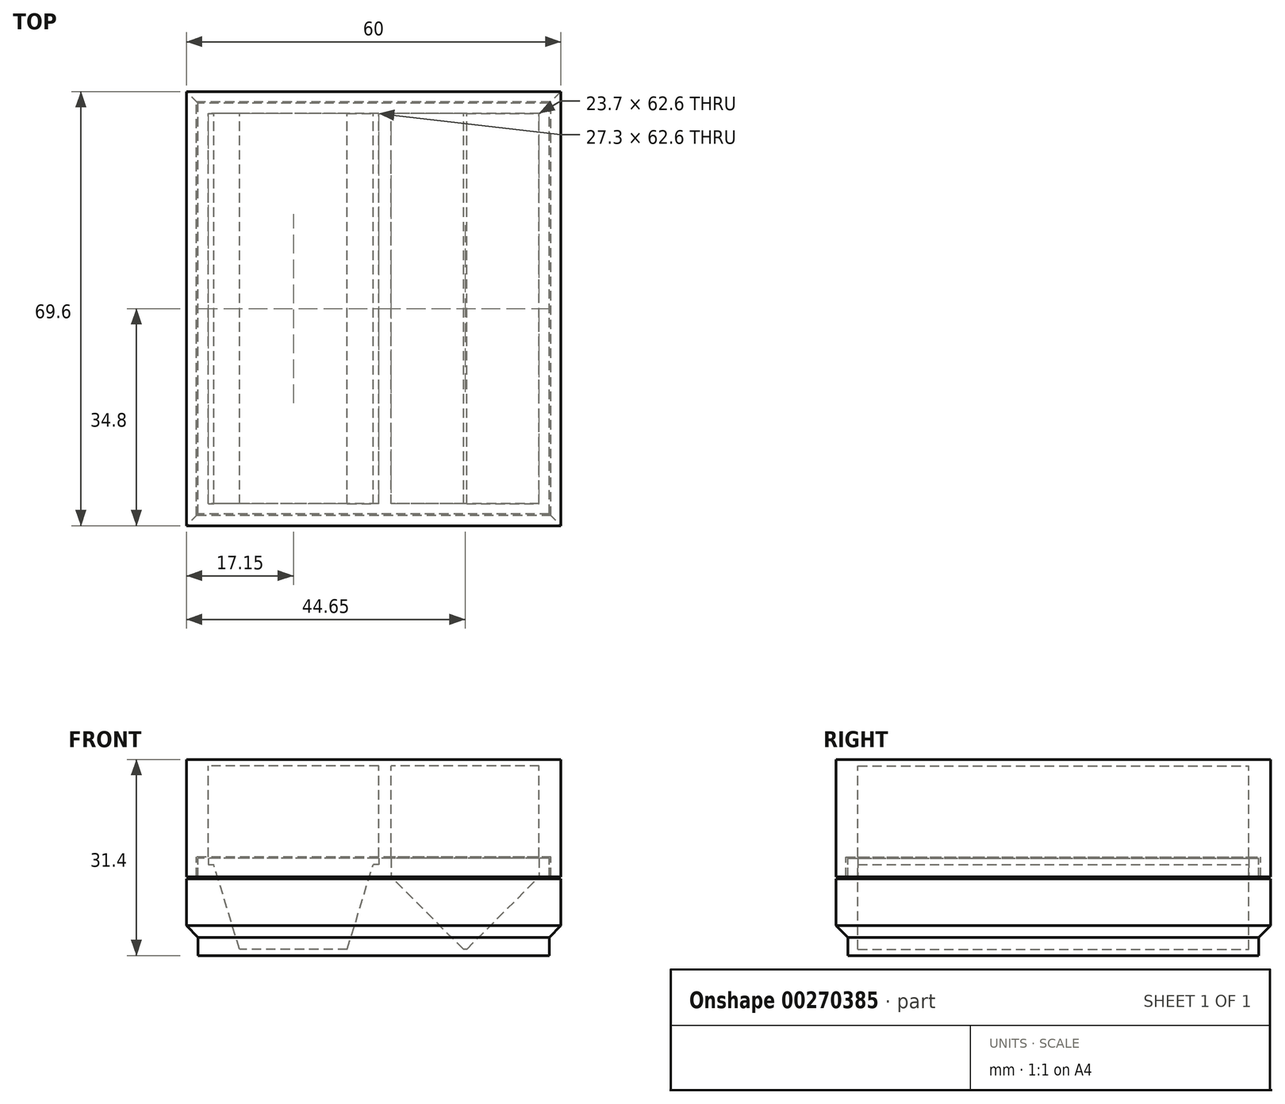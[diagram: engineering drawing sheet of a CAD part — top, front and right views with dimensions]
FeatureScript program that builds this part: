
annotation { "Feature Type Name" : "Feature", "Feature Type Description" : "" }
export const myFeature = defineFeature(function(context is Context, id is Id, definition is map)
    precondition{}
    {
        {
            assignVariable(context, id + "F0", {"name" : "chaff", "anyValue" : .3});
        }
        {
            assignVariable(context, id + "F1", {"name" : "basethick", "anyValue" : 1});
        }
        {
            assignVariable(context, id + "F2", {"name" : "wallthick", "anyValue" : 3.5});
        }
        {
            assignVariable(context, id + "F3", {"name" : "fiveTokenHeight", "anyValue" : 28});
        }
        {
            assignVariable(context, id + "F4", {"name" : "lidrimthick", "anyValue" : getVariable(context, 'wallthick') / 2 + (getVariable(context, 'chaff') / 2)});
        }
        {
            assignVariable(context, id + "F5", {"name" : "lidrimdepth", "anyValue" : 3});
        }
        {
            var Q0;
            Q0=qCreatedBy(makeId("Top.planeOp"),FACE);
            var sketch = newSketch(context, id + "F6", { "sketchPlane" : qUnion([Q0])});
            skLineSegment(sketch, "E0.bottom", {"start": v(30, -34.8) * mm, "end": v(-30, -34.8) * mm});
            skLineSegment(sketch, "E0.top", {"start": v(30, 34.8) * mm, "end": v(-30, 34.8) * mm});
            skLineSegment(sketch, "E0.left", {"start": v(30, -34.8) * mm, "end": v(30, 34.8) * mm});
            skLineSegment(sketch, "E0.right", {"start": v(-30, -34.8) * mm, "end": v(-30, 34.8) * mm});
            skPoint(sketch, "E0.middle", {"position": v(0, 0) * mm});
            skSolve(sketch);
        }
        {
            var Q0;
            Q0=qSketchRegion(id+"F6",true);
            extrude(context, id + "F7", {"entities" : qUnion([Q0]), "depth" : (getVariable(context, 'basethick')) * mm});
        }
        {
            var Q0;
            Q0=makeQuery(id+"F7.opExtrude","CAP_FACE",FACE,{"disambiguationData":[OSD([sQuery(id+"F6.wireOp",EDGE,"E0.bottom"),sQuery(id+"F6.wireOp",EDGE,"E0.top"),sQuery(id+"F6.wireOp",EDGE,"E0.left"),sQuery(id+"F6.wireOp",EDGE,"E0.right")])],"isStart":false});
            var sketch = newSketch(context, id + "F8", { "sketchPlane" : qUnion([Q0])});
            skLineSegment(sketch, "E1.bottom", {"start": v(26.5, -31.3) * mm, "end": v(-26.5, -31.3) * mm});
            skLineSegment(sketch, "E1.top", {"start": v(26.5, 31.3) * mm, "end": v(-26.5, 31.3) * mm});
            skLineSegment(sketch, "E1.left", {"start": v(26.5, -31.3) * mm, "end": v(26.5, 31.3) * mm});
            skLineSegment(sketch, "E1.right", {"start": v(-26.5, -31.3) * mm, "end": v(-26.5, 31.3) * mm});
            skPoint(sketch, "E1.middle", {"position": v(0, 0) * mm});
            skLineSegment(sketch, "E2", {"start": v(0, 31.3) * mm, "end": v(0, 34.8) * mm, "construction": true});
            skLineSegment(sketch, "E3.0", {"start": v(-30, -34.8) * mm, "end": v(-30, 34.8) * mm});
            skLineSegment(sketch, "E4.0", {"start": v(30, -34.8) * mm, "end": v(-30, -34.8) * mm});
            skLineSegment(sketch, "E5.0", {"start": v(30, -34.8) * mm, "end": v(30, 34.8) * mm});
            skLineSegment(sketch, "E6.0", {"start": v(30, 34.8) * mm, "end": v(-30, 34.8) * mm});
            skLineSegment(sketch, "E7", {"start": v(-30, 0) * mm, "end": v(-26.5, 0) * mm, "construction": true});
            skSolve(sketch);
        }
        {
            var Q0;
            Q0=qSketchRegion(id+"F8",true);
            extrude(context, id + "F9", {"entities" : qUnion([Q0]), "operationType" : NewBodyOperationType.ADD, "depth" : (getVariable(context, 'fiveTokenHeight') / 2 + getVariable(context, 'chaff') * 2) * mm});
        }
        {
            var Q0;
            Q0=makeQuery(id+"F9.opExtrude","SWEPT_FACE",FACE,{"disambiguationData":[OSD([sQuery(id+"F8.wireOp",EDGE,"E1.top")])]});
            var sketch = newSketch(context, id + "F10", { "sketchPlane" : qUnion([Q0])});
            skLineSegment(sketch, "E8", {"start": v(-26.5, 15.6) * mm, "end": v(0.8, 15.6) * mm, "construction": true});
            skLineSegment(sketch, "E9.bottom", {"start": v(0.8, 15.6) * mm, "end": v(2.8, 15.6) * mm});
            skLineSegment(sketch, "E9.top", {"start": v(0.8, 1) * mm, "end": v(2.8, 1) * mm});
            skLineSegment(sketch, "E9.left", {"start": v(0.8, 15.6) * mm, "end": v(0.8, 1) * mm});
            skLineSegment(sketch, "E9.right", {"start": v(2.8, 15.6) * mm, "end": v(2.8, 1) * mm});
            skLineSegment(sketch, "E10", {"start": v(2.8, 15.6) * mm, "end": v(26.5, 15.6) * mm, "construction": true});
            skLineSegment(sketch, "E11", {"start": v(-21.47, 1) * mm, "end": v(-4.22, 1) * mm});
            skPoint(sketch, "E12", {"position": v(-12.85, 1) * mm});
            skLineSegment(sketch, "E13", {"start": v(-12.85, 15.6) * mm, "end": v(-12.85, 1) * mm, "construction": true});
            skLineSegment(sketch, "E14", {"start": v(-21.47, 1) * mm, "end": v(-26.5, 1) * mm});
            skLineSegment(sketch, "E15", {"start": v(-26.5, 1) * mm, "end": v(-26.5, 15.6) * mm});
            skLineSegment(sketch, "E16", {"start": v(0.8, 1) * mm, "end": v(-4.22, 1) * mm});
            skLineSegment(sketch, "E17", {"start": v(14.65, 15.6) * mm, "end": v(14.65, 1) * mm, "construction": true});
            skLineSegment(sketch, "E18", {"start": v(14.4, 1) * mm, "end": v(14.9, 1) * mm});
            skLineSegment(sketch, "E19", {"start": v(14.4, 1) * mm, "end": v(2.8, 12.6) * mm});
            skLineSegment(sketch, "E20", {"start": v(14.9, 1) * mm, "end": v(26.5, 12.6) * mm});
            skLineSegment(sketch, "E21", {"start": v(2.8, 1) * mm, "end": v(14.4, 1) * mm});
            skLineSegment(sketch, "E22", {"start": v(14.9, 1) * mm, "end": v(26.5, 1) * mm});
            skLineSegment(sketch, "E23", {"start": v(26.5, 1) * mm, "end": v(26.5, 12.6) * mm});
            skLineSegment(sketch, "E24", {"start": v(-21.47, 1) * mm, "end": v(-26.5, 17.5) * mm});
            skLineSegment(sketch, "E25", {"start": v(-4.22, 1) * mm, "end": v(0.8, 17.5) * mm});
            skLineSegment(sketch, "E26", {"start": v(-26.5, 14.6) * mm, "end": v(-25.62, 14.6) * mm});
            skLineSegment(sketch, "E27", {"start": v(-26.5, 15.6) * mm, "end": v(-26.5, 14.6) * mm, "construction": true});
            skLineSegment(sketch, "E28.MirrorCS", {"start": v(0.8, 14.6) * mm, "end": v(-0.08, 14.6) * mm});
            skSolve(sketch);
        }
        {
            var Q0;
            {var subQ4=sQuery(id+"F10.wireOp",EDGE,"E9.bottom");Q0=makeQuery(id+"F10.imprint","IMPRINT",FACE,{"disambiguationData":[TD([[makeQuery(id+"F10.imprint","IMPRINT",EDGE,{"derivedFrom":subQ4}),1.0]])]});}
            var Q1;
            Q1=makeQuery(id+"F9.opExtrude","SWEPT_FACE",FACE,{"disambiguationData":[OSD([sQuery(id+"F8.wireOp",EDGE,"E1.bottom")])]});
            extrude(context, id + "F11", {"entities" : qUnion([Q0]), "operationType" : NewBodyOperationType.ADD, "endBound" : BoundingType.UP_TO_SURFACE, "endBoundEntityFace" : qUnion([Q1]), "depth" : 25 * mm});
        }
        {
            var Q0;
            {var subQ0=sQuery(id+"F10.wireOp",EDGE,"b7063ba6-163c-4e90-9692-3a0a1676d49b.0");var subQ1=sQuery(id+"F10.wireOp",EDGE,"5b0bd29a-2a72-4641-92b4-ce3cebaaf724.1.0.1");var subQ2=sQuery(id+"F10.wireOp",EDGE,"5b0bd29a-2a72-4641-92b4-ce3cebaaf724.2.0.1");Q0=makeQuery(id+"F11.boolean.opBoolean","MERGE",FACE,{"derivedFrom":[makeQuery(id+"F9.opExtrude","CAP_FACE",FACE,{"disambiguationData":[OSD([sQuery(id+"F8.wireOp",EDGE,"E1.bottom"),sQuery(id+"F8.wireOp",EDGE,"E1.top"),sQuery(id+"F8.wireOp",EDGE,"E1.left"),sQuery(id+"F8.wireOp",EDGE,"E1.right"),sQuery(id+"F8.wireOp",EDGE,"E3.0"),sQuery(id+"F8.wireOp",EDGE,"E4.0"),sQuery(id+"F8.wireOp",EDGE,"E5.0"),sQuery(id+"F8.wireOp",EDGE,"E6.0")])],"isStart":false}),makeQuery(id+"F11.opExtrude","SWEPT_FACE",FACE,{"disambiguationData":[OSD([subQ0]),TDD([makeQuery(id+"F10.imprint","IMPRINT",EDGE,{"disambiguationData":[TD([[makeQuery(id+"F10.imprint","INTERSECT",VERTEX,{"derivedFrom":[sQuery(id+"F10.wireOp",EDGE,"ed8556cc-012e-414f-a647-4d99696943b9.0"),subQ0]}),-1.0]])],"derivedFrom":subQ0})])]}),makeQuery(id+"F11.opExtrude","SWEPT_FACE",FACE,{"disambiguationData":[OSD([subQ0]),TDD([makeQuery(id+"F10.imprint","IMPRINT",EDGE,{"disambiguationData":[TD([[makeQuery(id+"F10.imprint","INTERSECT",VERTEX,{"disambiguationData":[OD(1.0)],"derivedFrom":[subQ2,subQ0]}),1.0]])],"derivedFrom":subQ0})])]}),makeQuery(id+"F11.opExtrude","SWEPT_FACE",FACE,{"disambiguationData":[OSD([subQ0]),TDD([makeQuery(id+"F10.imprint","IMPRINT",EDGE,{"disambiguationData":[TD([[makeQuery(id+"F10.imprint","INTERSECT",VERTEX,{"disambiguationData":[OD(1.0)],"derivedFrom":[subQ1,subQ0]}),1.0]])],"derivedFrom":subQ0})])]}),makeQuery(id+"F11.opExtrude","SWEPT_FACE",FACE,{"disambiguationData":[OSD([subQ0]),TDD([makeQuery(id+"F10.imprint","IMPRINT",EDGE,{"disambiguationData":[TD([[makeQuery(id+"F10.imprint","INTERSECT",VERTEX,{"derivedFrom":[sQuery(id+"F10.wireOp",EDGE,"CCxmkI6E-hdHg-CZTa-q9Gf-agiM700yoBqG"),subQ0]}),1.0]])],"derivedFrom":subQ0})])]})]});}
            cPlane(context, id + "F12", {"entities" : qUnion([Q0]), "cplaneType" : CPlaneType.OFFSET, "offset" : .1 * mm, "width" : 150 * mm, "height" : 150 * mm});
        }
        {
            var Q0;
            Q0=makeQuery(id+"F7.opExtrude","SWEPT_BODY",BODY,{"disambiguationData":[OSD([sQuery(id+"F6.wireOp",EDGE,"E0.bottom"),sQuery(id+"F6.wireOp",EDGE,"E0.top"),sQuery(id+"F6.wireOp",EDGE,"E0.left"),sQuery(id+"F6.wireOp",EDGE,"E0.right")])]});
            var Q1;
            Q1=qCreatedBy(id+"F12.planeOp",FACE);
            mirror(context, id + "F13", {"entities" : qUnion([Q0]), "mirrorPlane" : qUnion([Q1])});
        }
        {
            var Q0;
            {var subQ0=sQuery(id+"F10.wireOp",EDGE,"b7063ba6-163c-4e90-9692-3a0a1676d49b.0");var subQ1=sQuery(id+"F10.wireOp",EDGE,"5b0bd29a-2a72-4641-92b4-ce3cebaaf724.1.0.1");var subQ2=sQuery(id+"F10.wireOp",EDGE,"5b0bd29a-2a72-4641-92b4-ce3cebaaf724.2.0.1");Q0=makeQuery(id+"F11.boolean.opBoolean","MERGE",FACE,{"derivedFrom":[makeQuery(id+"F9.opExtrude","CAP_FACE",FACE,{"disambiguationData":[OSD([sQuery(id+"F8.wireOp",EDGE,"E1.bottom"),sQuery(id+"F8.wireOp",EDGE,"E1.top"),sQuery(id+"F8.wireOp",EDGE,"E1.left"),sQuery(id+"F8.wireOp",EDGE,"E1.right"),sQuery(id+"F8.wireOp",EDGE,"E3.0"),sQuery(id+"F8.wireOp",EDGE,"E4.0"),sQuery(id+"F8.wireOp",EDGE,"E5.0"),sQuery(id+"F8.wireOp",EDGE,"E6.0")])],"isStart":false}),makeQuery(id+"F11.opExtrude","SWEPT_FACE",FACE,{"disambiguationData":[OSD([subQ0]),TDD([makeQuery(id+"F10.imprint","IMPRINT",EDGE,{"disambiguationData":[TD([[makeQuery(id+"F10.imprint","INTERSECT",VERTEX,{"derivedFrom":[sQuery(id+"F10.wireOp",EDGE,"ed8556cc-012e-414f-a647-4d99696943b9.0"),subQ0]}),-1.0]])],"derivedFrom":subQ0})])]}),makeQuery(id+"F11.opExtrude","SWEPT_FACE",FACE,{"disambiguationData":[OSD([subQ0]),TDD([makeQuery(id+"F10.imprint","IMPRINT",EDGE,{"disambiguationData":[TD([[makeQuery(id+"F10.imprint","INTERSECT",VERTEX,{"disambiguationData":[OD(1.0)],"derivedFrom":[subQ2,subQ0]}),1.0]])],"derivedFrom":subQ0})])]}),makeQuery(id+"F11.opExtrude","SWEPT_FACE",FACE,{"disambiguationData":[OSD([subQ0]),TDD([makeQuery(id+"F10.imprint","IMPRINT",EDGE,{"disambiguationData":[TD([[makeQuery(id+"F10.imprint","INTERSECT",VERTEX,{"disambiguationData":[OD(1.0)],"derivedFrom":[subQ1,subQ0]}),1.0]])],"derivedFrom":subQ0})])]}),makeQuery(id+"F11.opExtrude","SWEPT_FACE",FACE,{"disambiguationData":[OSD([subQ0]),TDD([makeQuery(id+"F10.imprint","IMPRINT",EDGE,{"disambiguationData":[TD([[makeQuery(id+"F10.imprint","INTERSECT",VERTEX,{"derivedFrom":[sQuery(id+"F10.wireOp",EDGE,"CCxmkI6E-hdHg-CZTa-q9Gf-agiM700yoBqG"),subQ0]}),1.0]])],"derivedFrom":subQ0})])]})]});}
            var sketch = newSketch(context, id + "F14", { "sketchPlane" : qUnion([Q0])});
            skLineSegment(sketch, "E29.0", {"start": v(30, 34.8) * mm, "end": v(-30, 34.8) * mm});
            skLineSegment(sketch, "E30.0", {"start": v(-30, -34.8) * mm, "end": v(-30, 34.8) * mm});
            skLineSegment(sketch, "E31.0", {"start": v(30, -34.8) * mm, "end": v(-30, -34.8) * mm});
            skLineSegment(sketch, "E32.0", {"start": v(30, -34.8) * mm, "end": v(30, 34.8) * mm});
            skLineSegment(sketch, "E33.0", {"start": v(28.1, 32.9) * mm, "end": v(-28.1, 32.9) * mm});
            skLineSegment(sketch, "E33.1", {"start": v(28.1, -32.9) * mm, "end": v(28.1, 32.9) * mm});
            skLineSegment(sketch, "E33.2", {"start": v(28.1, -32.9) * mm, "end": v(-28.1, -32.9) * mm});
            skLineSegment(sketch, "E33.3", {"start": v(-28.1, -32.9) * mm, "end": v(-28.1, 32.9) * mm});
            skSolve(sketch);
        }
        {
            var Q0;
            Q0=makeQuery(id+"F14.imprint","IMPRINT",FACE,{"disambiguationData":[TD([[makeQuery(id+"F14.imprint","IMPRINT",EDGE,{"derivedFrom":sQuery(id+"F14.wireOp",EDGE,"E29.0")}),1.0]])]});
            extrude(context, id + "F15", {"entities" : qUnion([Q0]), "operationType" : NewBodyOperationType.REMOVE, "oppositeDirection" : true, "depth" : (getVariable(context, 'lidrimdepth') + getVariable(context, 'chaff')) * mm});
        }
        {
            var Q0;
            Q0=makeQuery(id+"F7.opExtrude","CAP_FACE",FACE,{"disambiguationData":[OSD([sQuery(id+"F6.wireOp",EDGE,"E0.bottom"),sQuery(id+"F6.wireOp",EDGE,"E0.top"),sQuery(id+"F6.wireOp",EDGE,"E0.left"),sQuery(id+"F6.wireOp",EDGE,"E0.right")])],"isStart":true});
            var sketch = newSketch(context, id + "F16", { "sketchPlane" : qUnion([Q0])});
            skLineSegment(sketch, "E34.0", {"start": v(30, 34.8) * mm, "end": v(-30, 34.8) * mm});
            skLineSegment(sketch, "E35.0", {"start": v(-30, 34.8) * mm, "end": v(-30, -34.8) * mm});
            skLineSegment(sketch, "E36.0", {"start": v(30, 34.8) * mm, "end": v(30, -34.8) * mm});
            skLineSegment(sketch, "E37.0", {"start": v(30, -34.8) * mm, "end": v(-30, -34.8) * mm});
            skLineSegment(sketch, "E38.0", {"start": v(28.1, 32.9) * mm, "end": v(-28.1, 32.9) * mm});
            skLineSegment(sketch, "E38.1", {"start": v(28.1, 32.9) * mm, "end": v(28.1, -32.9) * mm});
            skLineSegment(sketch, "E38.2", {"start": v(28.1, -32.9) * mm, "end": v(-28.1, -32.9) * mm});
            skLineSegment(sketch, "E38.3", {"start": v(-28.1, 32.9) * mm, "end": v(-28.1, -32.9) * mm});
            skSolve(sketch);
        }
        {
            var Q0;
            Q0=qSketchRegion(id+"F16",true);
            extrude(context, id + "F17", {"entities" : qUnion([Q0]), "operationType" : NewBodyOperationType.REMOVE, "oppositeDirection" : true, "depth" : (getVariable(context, 'lidrimthick') + 3) * mm});
        }
        {
            var Q0;
            Q0=makeQuery(id+"F17.boolean.opBoolean","COPY",EDGE,{"derivedFrom":makeQuery(id+"F17.opExtrude","CAP_EDGE",EDGE,{"disambiguationData":[OSD([sQuery(id+"F16.wireOp",EDGE,"E38.0")])],"isStart":false})});
            var Q1;
            Q1=makeQuery(id+"F17.boolean.opBoolean","COPY",EDGE,{"derivedFrom":makeQuery(id+"F17.opExtrude","CAP_EDGE",EDGE,{"disambiguationData":[OSD([sQuery(id+"F16.wireOp",EDGE,"E38.3")])],"isStart":false})});
            var Q2;
            Q2=makeQuery(id+"F17.boolean.opBoolean","COPY",EDGE,{"derivedFrom":makeQuery(id+"F17.opExtrude","CAP_EDGE",EDGE,{"disambiguationData":[OSD([sQuery(id+"F16.wireOp",EDGE,"E38.2")])],"isStart":false})});
            var Q3;
            Q3=makeQuery(id+"F17.boolean.opBoolean","COPY",EDGE,{"derivedFrom":makeQuery(id+"F17.opExtrude","CAP_EDGE",EDGE,{"disambiguationData":[OSD([sQuery(id+"F16.wireOp",EDGE,"E38.1")])],"isStart":false})});
            chamfer(context, id + "F18", {"entities" : qUnion([Q0, Q1, Q2, Q3]), "width" : 2 * mm, "tangentPropagation" : true});
        }
        {
            var Q0;
            {var subQ0=sQuery(id+"F10.wireOp",EDGE,"b7063ba6-163c-4e90-9692-3a0a1676d49b.0");var subQ1=sQuery(id+"F10.wireOp",EDGE,"5b0bd29a-2a72-4641-92b4-ce3cebaaf724.1.0.1");var subQ2=sQuery(id+"F10.wireOp",EDGE,"5b0bd29a-2a72-4641-92b4-ce3cebaaf724.2.0.1");Q0=makeQuery(id+"F13.opPattern","COPY",FACE,{"derivedFrom":makeQuery(id+"F11.boolean.opBoolean","MERGE",FACE,{"derivedFrom":[makeQuery(id+"F9.opExtrude","CAP_FACE",FACE,{"disambiguationData":[OSD([sQuery(id+"F8.wireOp",EDGE,"E1.bottom"),sQuery(id+"F8.wireOp",EDGE,"E1.top"),sQuery(id+"F8.wireOp",EDGE,"E1.left"),sQuery(id+"F8.wireOp",EDGE,"E1.right"),sQuery(id+"F8.wireOp",EDGE,"E3.0"),sQuery(id+"F8.wireOp",EDGE,"E4.0"),sQuery(id+"F8.wireOp",EDGE,"E5.0"),sQuery(id+"F8.wireOp",EDGE,"E6.0")])],"isStart":false}),makeQuery(id+"F11.opExtrude","SWEPT_FACE",FACE,{"disambiguationData":[OSD([subQ0]),TDD([makeQuery(id+"F10.imprint","IMPRINT",EDGE,{"disambiguationData":[TD([[makeQuery(id+"F10.imprint","INTERSECT",VERTEX,{"derivedFrom":[sQuery(id+"F10.wireOp",EDGE,"ed8556cc-012e-414f-a647-4d99696943b9.0"),subQ0]}),-1.0]])],"derivedFrom":subQ0})])]}),makeQuery(id+"F11.opExtrude","SWEPT_FACE",FACE,{"disambiguationData":[OSD([subQ0]),TDD([makeQuery(id+"F10.imprint","IMPRINT",EDGE,{"disambiguationData":[TD([[makeQuery(id+"F10.imprint","INTERSECT",VERTEX,{"disambiguationData":[OD(1.0)],"derivedFrom":[subQ2,subQ0]}),1.0]])],"derivedFrom":subQ0})])]}),makeQuery(id+"F11.opExtrude","SWEPT_FACE",FACE,{"disambiguationData":[OSD([subQ0]),TDD([makeQuery(id+"F10.imprint","IMPRINT",EDGE,{"disambiguationData":[TD([[makeQuery(id+"F10.imprint","INTERSECT",VERTEX,{"disambiguationData":[OD(1.0)],"derivedFrom":[subQ1,subQ0]}),1.0]])],"derivedFrom":subQ0})])]}),makeQuery(id+"F11.opExtrude","SWEPT_FACE",FACE,{"disambiguationData":[OSD([subQ0]),TDD([makeQuery(id+"F10.imprint","IMPRINT",EDGE,{"disambiguationData":[TD([[makeQuery(id+"F10.imprint","INTERSECT",VERTEX,{"derivedFrom":[sQuery(id+"F10.wireOp",EDGE,"CCxmkI6E-hdHg-CZTa-q9Gf-agiM700yoBqG"),subQ0]}),1.0]])],"derivedFrom":subQ0})])]})]}),"instanceName":"1"});}
            var sketch = newSketch(context, id + "F19", { "sketchPlane" : qUnion([Q0])});
            skPoint(sketch, "E39.0", {"position": v(-26.5, 31.3) * mm});
            skPoint(sketch, "E40.0", {"position": v(26.5, -31.3) * mm});
            skPoint(sketch, "E41.0", {"position": v(-26.5, -31.3) * mm});
            skLineSegment(sketch, "E42", {"start": v(26.5, 31.3) * mm, "end": v(-26.5, 31.3) * mm, "construction": true});
            skLineSegment(sketch, "E43", {"start": v(-26.5, -31.3) * mm, "end": v(26.5, -31.3) * mm, "construction": true});
            skLineSegment(sketch, "E44", {"start": v(26.5, 31.3) * mm, "end": v(26.5, -31.3) * mm, "construction": true});
            skLineSegment(sketch, "E45", {"start": v(-26.5, 31.3) * mm, "end": v(-26.5, -31.3) * mm, "construction": true});
            skLineSegment(sketch, "E46.0", {"start": v(28.4, 33.2) * mm, "end": v(-28.4, 33.2) * mm});
            skLineSegment(sketch, "E46.1", {"start": v(28.4, 33.2) * mm, "end": v(28.4, -33.2) * mm});
            skLineSegment(sketch, "E46.2", {"start": v(-28.4, -33.2) * mm, "end": v(28.4, -33.2) * mm});
            skLineSegment(sketch, "E46.3", {"start": v(-28.4, 33.2) * mm, "end": v(-28.4, -33.2) * mm});
            skLineSegment(sketch, "E47.0", {"start": v(30, 34.8) * mm, "end": v(-30, 34.8) * mm});
            skLineSegment(sketch, "E48.0", {"start": v(30, 34.8) * mm, "end": v(30, -34.8) * mm});
            skLineSegment(sketch, "E49.0", {"start": v(30, -34.8) * mm, "end": v(-30, -34.8) * mm});
            skLineSegment(sketch, "E50.0", {"start": v(-30, 34.8) * mm, "end": v(-30, -34.8) * mm});
            skPoint(sketch, "E51", {"position": v(26.5, 31.3) * mm});
            skSolve(sketch);
        }
        {
            var Q0;
            Q0=qSketchRegion(id+"F19",true);
            extrude(context, id + "F20", {"entities" : qUnion([Q0]), "operationType" : NewBodyOperationType.ADD, "depth" : 3.2 * mm});
        }
        {
            var Q0;
            {var subQ2=sQuery(id+"F10.wireOp",EDGE,"E19");Q0=makeQuery(id+"F10.imprint","IMPRINT",FACE,{"disambiguationData":[TD([[makeQuery(id+"F10.imprint","IMPRINT",EDGE,{"derivedFrom":subQ2}),1.0]])]});}
            var Q1;
            Q1=makeQuery(id+"F10.imprint","IMPRINT",FACE,{"disambiguationData":[TD([[makeQuery(id+"F10.imprint","IMPRINT",EDGE,{"derivedFrom":sQuery(id+"F10.wireOp",EDGE,"E20")}),-1.0]])]});
            var Q2;
            {var subQ0=sQuery(id+"F10.wireOp",EDGE,"E14");Q2=makeQuery(id+"F10.imprint","IMPRINT",FACE,{"disambiguationData":[TD([[makeQuery(id+"F10.imprint","IMPRINT",EDGE,{"derivedFrom":subQ0}),-1.0]])]});}
            var Q3;
            {var subQ0=sQuery(id+"F10.wireOp",EDGE,"E16");Q3=makeQuery(id+"F10.imprint","IMPRINT",FACE,{"disambiguationData":[TD([[makeQuery(id+"F10.imprint","IMPRINT",EDGE,{"derivedFrom":subQ0}),-1.0]])]});}
            var Q4;
            {var subQ0=sQuery(id+"F8.wireOp",EDGE,"E1.right");var subQ1=sQuery(id+"F8.wireOp",EDGE,"E1.bottom");Q4=makeQuery(id+"F11.boolean.opBoolean","SPLIT",FACE,{"disambiguationData":[TD([makeQuery(id+"F9.opExtrude","SWEPT_FACE",FACE,{"disambiguationData":[OSD([subQ0])]})])],"derivedFrom":makeQuery(id+"F9.opExtrude","SWEPT_FACE",FACE,{"disambiguationData":[OSD([subQ1])]})});}
            extrude(context, id + "F21", {"entities" : qUnion([Q0, Q1, Q2, Q3]), "operationType" : NewBodyOperationType.ADD, "endBound" : BoundingType.UP_TO_SURFACE, "endBoundEntityFace" : qUnion([Q4]), "depth" : 25 * mm});
        }
    });
